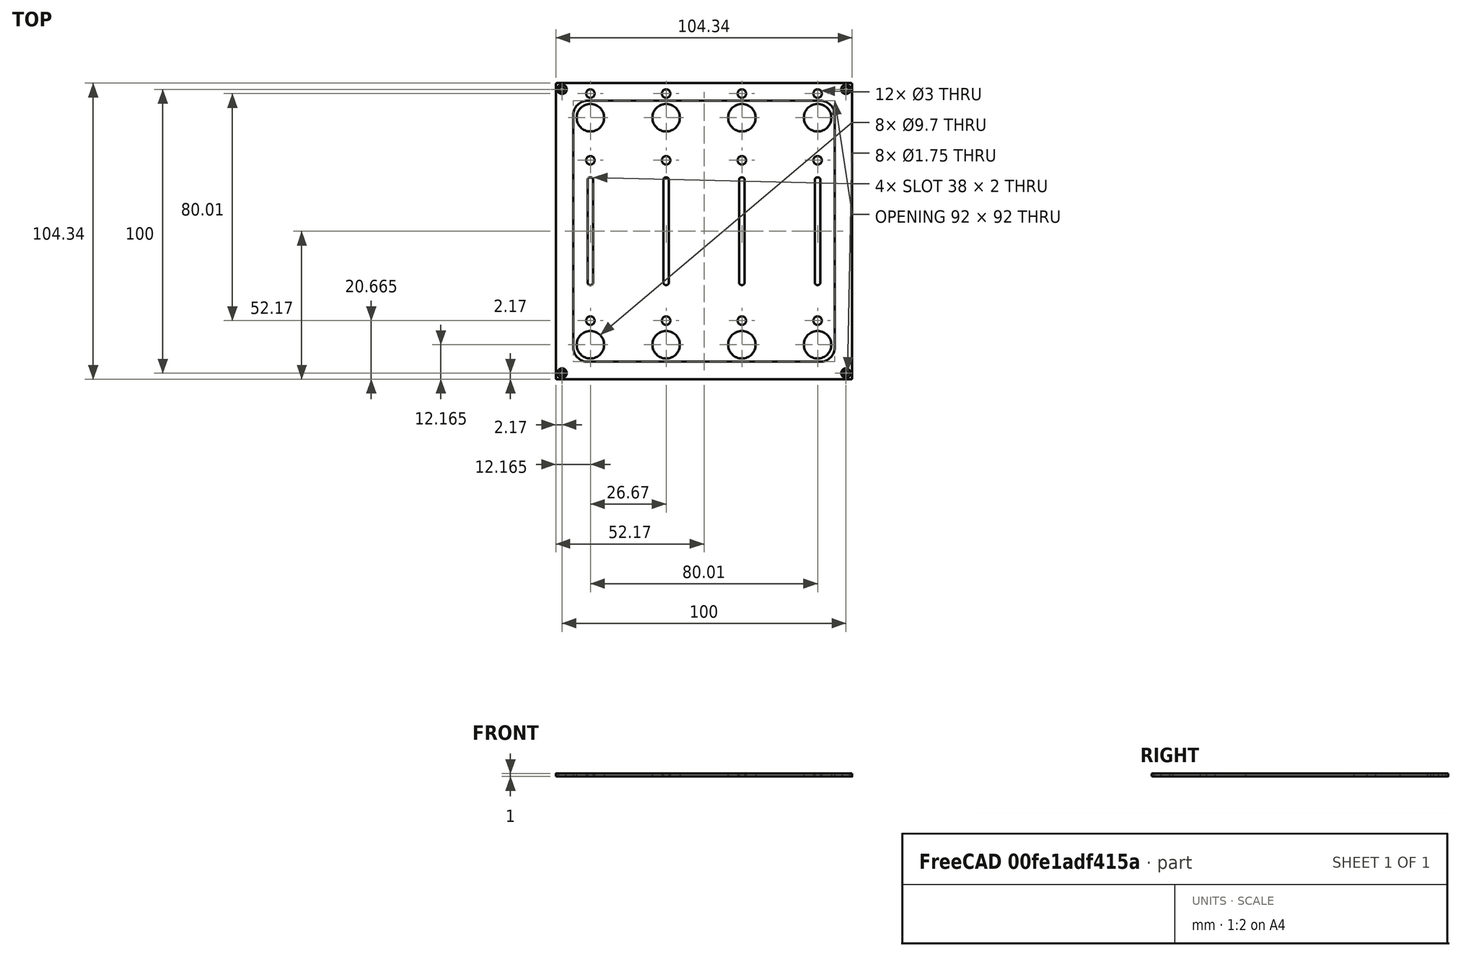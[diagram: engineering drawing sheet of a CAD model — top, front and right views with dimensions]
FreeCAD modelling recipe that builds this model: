
FCSTD DOCUMENT  (FreeCAD 0.21R33668 +26 (Git))
Label: grid_frontpanel
License: All rights reserved
LicenseURL: http://en.wikipedia.org/wiki/All_rights_reserved
objects: Sketcher::SketchObject×10, PartDesign::Hole×6, TechDraw::DrawProjGroupItem×4, PartDesign::Pocket×3, PartDesign::Body×3, TechDraw::DrawViewDimension×3, PartDesign::FeatureBase×2, TechDraw::DrawRichAnno×2, Spreadsheet::Sheet×1, PartDesign::Pad×1, TechDraw::DrawSVGTemplate×1, TechDraw::DrawProjGroup×1, TechDraw::DrawPage×1
note: 35 computed .brp shape members not serialized (recipe doc carries the construction recipe); baked Part::Feature solids carry a one-line shape summary decoded from their .brp

FEATURE [Spreadsheet::Sheet] Spreadsheet  label="dim"
  cells = A1='panel_length; B1(panel_length)=104.35; A2='panel_thickness; B2(panel_thickness)=1; A3='panel_radius; B3(panel_radius)==(104.35 - 103.6) / 2; A5='corner_drill_dist; B5(corner_drill_dist)=100; A6='corner_drill_dia; B6(corner_drill_dia)=1.75; A7='corner_drill_countersink; B7(corner_drill_countersink)=3.3; A9='undercut_width; B9(undercut_width)=1; A10='undercut_length; B10(undercut_length)=90; A11='undercut_offset; B11(undercut_offset)=1; A12='undercut_depth; B12(undercut_depth)=0.8; A14='ui_raster; B14(ui_raster)=26.67; A16='light_drill_dia; B16(light_drill_dia)=3; D16='old 2.9; A17='light_bore_dia; B17(light_bore_dia)=3.45; C17='check; D17='old 3.30; E17='DEPRICATED; A18='light_bore_depth; B18(light_bore_depth)=0.4; C18='check; D18='old 0.40; E18='DEPRICATED; A20='pot_drill_dia; B20(pot_drill_dia)=9.7; C20='check; D20='old 6.20; A21='pot_led_dist; B21(pot_led_dist)=8.5; B22=0; A23='but_drill_dia; B23(but_drill_dia)=9.7; A24='but_led_dist; B24(but_led_dist)=8.5; A26='fad_cutout_width; B26(fad_cutout_width)=2; C26='check; D26='old 1.50; A27='fad_cutout_length; B27(fad_cutout_length)=36; A28='fad_led_dist; B28(fad_led_dist)=25; A30='enc_drill_dia; B30(enc_drill_dia)=9.7; C30='check; D30='old 6.20; A31='enc_led_dist; B31(enc_led_dist)=8.5; A33='longfad_cutout_width; B33(longfad_cutout_width)=2; A34='longfad_cutout_length; B34(longfad_cutout_length)=66; A36='panel_chamfer; B36(panel_chamfer)=0.2; C36='UPDATE DRAWING
FEATURE [Sketcher::SketchObject] Sketch
  FullyConstrained = true
  MapMode = 5
  Support = -> [XY_Plane]
  expr: Constraints[12] = <<dim>>.panel_radius
  expr: Constraints[16] = <<dim>>.panel_length
  sketch-geometry (11):
    g0: LineSegment StartX=-51.8 StartY=52.175 StartZ=0 EndX=51.8 EndY=52.175 EndZ=0
    g1: LineSegment StartX=52.175 StartY=51.8 StartZ=0 EndX=52.175 EndY=-51.8 EndZ=0
    g2: LineSegment StartX=51.8 StartY=-52.175 StartZ=0 EndX=-51.8 EndY=-52.175 EndZ=0
    g3: LineSegment StartX=-52.175 StartY=-51.8 StartZ=0 EndX=-52.175 EndY=51.8 EndZ=0
    g4: ArcOfCircle CenterX=-51.8 CenterY=51.8 CenterZ=0 NormalX=0 NormalY=0 NormalZ=1 AngleXU=0 Radius=0.375 StartAngle=1.5708 EndAngle=3.14159
    g5: ArcOfCircle CenterX=51.8 CenterY=51.8 CenterZ=0 NormalX=0 NormalY=0 NormalZ=1 AngleXU=0 Radius=0.375 StartAngle=8.4e-15 EndAngle=1.5708
    g6: ArcOfCircle CenterX=51.8 CenterY=-51.8 CenterZ=0 NormalX=0 NormalY=0 NormalZ=1 AngleXU=0 Radius=0.375 StartAngle=4.71239 EndAngle=6.28319
    g7: ArcOfCircle CenterX=-51.8 CenterY=-51.8 CenterZ=0 NormalX=0 NormalY=0 NormalZ=1 AngleXU=0 Radius=0.375 StartAngle=3.14159 EndAngle=4.71239
    g8: LineSegment StartX=-51.8 StartY=51.8 StartZ=0 EndX=0 EndY=0 EndZ=0
    g9: LineSegment StartX=0 StartY=0 StartZ=0 EndX=51.8 EndY=51.8 EndZ=0
    g10: LineSegment StartX=0 StartY=0 StartZ=0 EndX=-51.8 EndY=-51.8 EndZ=0
  constraints (26):
    c: Horizontal(g0)
    c: Horizontal(g2)
    c: Vertical(g1)
    c: Vertical(g3)
    c: Tangent(g3,g4) = 1.5708
    c: Tangent(g0,g4) = 1.5708
    c: Tangent(g0,g5) = 1.5708
    c: Tangent(g1,g5) = 1.5708
    c: Tangent(g1,g6) = 1.5708
    c: Tangent(g2,g6) = 1.5708
    c: Tangent(g2,g7) = 1.5708
    c: Tangent(g3,g7) = 1.5708
    c: Radius(g4) = 0.375
    c: Equal(g4,g5)
    c: Equal(g4,g6)
    c: Equal(g4,g7)
    c: DistanceX(g3,g1) = 104.35
    c: Equal(g3,g0)
    c: Coincident(g8,g4)
    c: Coincident(g8,g-1)
    c: Coincident(g8,g9)
    c: Coincident(g9,g5)
    c: Coincident(g-1,g10)
    c: Coincident(g10,g7)
    c: Equal(g10,g8)
    c: Equal(g8,g9)
FEATURE [PartDesign::Pad] Pad  label="panel"
  AllowMultiFace = false
  Direction = (0,0,1)
  Length = 1
  Length2 = 100
  Profile = -> Sketch
  Reversed = true
  Type = 0
  expr: Length = <<dim>>.panel_thickness
FEATURE [Sketcher::SketchObject] Sketch001
  FullyConstrained = true
  MapMode = 5
  Support = -> [XY_Plane]
  expr: Constraints[13] = <<dim>>.corner_drill_dist
  sketch-geometry (9):
    g0: LineSegment StartX=-50 StartY=50 StartZ=0 EndX=-50 EndY=-50 EndZ=0
    g1: LineSegment StartX=-50 StartY=-50 StartZ=0 EndX=50 EndY=-50 EndZ=0
    g2: LineSegment StartX=50 StartY=-50 StartZ=0 EndX=50 EndY=50 EndZ=0
    g3: LineSegment StartX=50 StartY=50 StartZ=0 EndX=-50 EndY=50 EndZ=0
    g4: Circle CenterX=0 CenterY=0 CenterZ=0 NormalX=0 NormalY=0 NormalZ=1 AngleXU=0 Radius=70.7107
    g5: Circle CenterX=-50 CenterY=50 CenterZ=0 NormalX=0 NormalY=0 NormalZ=1 AngleXU=0 Radius=0.5
    g6: Circle CenterX=50 CenterY=50 CenterZ=0 NormalX=0 NormalY=0 NormalZ=1 AngleXU=0 Radius=0.5
    g7: Circle CenterX=50 CenterY=-50 CenterZ=0 NormalX=0 NormalY=0 NormalZ=1 AngleXU=0 Radius=0.5
    g8: Circle CenterX=-50 CenterY=-50 CenterZ=0 NormalX=0 NormalY=0 NormalZ=1 AngleXU=0 Radius=0.5
  constraints (22):
    c: Coincident(g0,g1)
    c: Coincident(g1,g2)
    c: Coincident(g2,g3)
    c: Coincident(g3,g0)
    c: Equal(g0,g1)
    c: Equal(g0,g2)
    c: Equal(g0,g3)
    c: PointOnObject(g0,g4)
    c: PointOnObject(g1,g4)
    c: PointOnObject(g2,g4)
    c: PointOnObject(g3,g4)
    c: Coincident(g4,g-1)
    c: Horizontal(g3)
    c: DistanceX(g3,g3) = 100
    c: Coincident(g5,g0)
    c: Coincident(g6,g2)
    c: Coincident(g7,g1)
    c: Coincident(g8,g0)
    c: Diameter(g8) = 1
    c: Equal(g8,g7)
    c: Equal(g8,g6)
    c: Equal(g8,g5)
FEATURE [Sketcher::SketchObject] Sketch002
  AttachmentOffset = pos=(0,0,-4.8) rot=(0,0,1;0rad)
  FullyConstrained = true
  MapMode = 5
  Placement = pos=(0,0,-4.8) rot=(0,0,1;0rad)
  Support = -> [XY_Plane]
  expr: .AttachmentOffset.Base.z = -<<dim>>.undercut_depth - 4
  expr: Constraints[91] = <<dim>>.undercut_length
  expr: Constraints[92] = <<dim>>.undercut_width
  expr: Constraints[93] = <<dim>>.panel_length / 2 - <<dim>>.undercut_offset - <<dim>>.undercut_width / 2
  sketch-geometry (40):
    g0: LineSegment StartX=-45 StartY=50.175 StartZ=0 EndX=45 EndY=50.175 EndZ=0
    g1: LineSegment StartX=-45 StartY=51.175 StartZ=0 EndX=45 EndY=51.175 EndZ=0
    g2: LineSegment StartX=-50.675 StartY=45 StartZ=0 EndX=0 EndY=0 EndZ=0
    g3: LineSegment StartX=0 StartY=0 StartZ=0 EndX=-50.675 EndY=-45 EndZ=0
    g4: LineSegment StartX=0 StartY=0 StartZ=0 EndX=-45 EndY=50.675 EndZ=0
    g5: LineSegment StartX=45 StartY=50.675 StartZ=0 EndX=0 EndY=0 EndZ=0
    g6: LineSegment StartX=0 StartY=0 StartZ=0 EndX=50.675 EndY=45 EndZ=0
    g7: LineSegment StartX=50.675 StartY=-45 StartZ=0 EndX=0 EndY=0 EndZ=0
    g8: LineSegment StartX=0 StartY=0 StartZ=0 EndX=45 EndY=-50.675 EndZ=0
    g9: LineSegment StartX=0 StartY=0 StartZ=0 EndX=-45 EndY=-50.675 EndZ=0
    g10: ArcOfCircle CenterX=45 CenterY=50.675 CenterZ=0 NormalX=0 NormalY=0 NormalZ=1 AngleXU=0 Radius=0.5 StartAngle=4.71239 EndAngle=6.28319
    g11: ArcOfCircle CenterX=45 CenterY=50.675 CenterZ=0 NormalX=0 NormalY=0 NormalZ=1 AngleXU=0 Radius=0.5 StartAngle=0 EndAngle=1.5708
    g12: LineSegment StartX=45 StartY=50.675 StartZ=0 EndX=45.5 EndY=50.675 EndZ=0
    g13: ArcOfCircle CenterX=-45 CenterY=50.675 CenterZ=0 NormalX=0 NormalY=0 NormalZ=1 AngleXU=0 Radius=0.5 StartAngle=3.14159 EndAngle=4.71239
    g14: ArcOfCircle CenterX=-45 CenterY=50.675 CenterZ=0 NormalX=0 NormalY=0 NormalZ=1 AngleXU=0 Radius=0.5 StartAngle=1.5708 EndAngle=3.14159
    g15: LineSegment StartX=-45.5 StartY=50.675 StartZ=0 EndX=-45 EndY=50.675 EndZ=0
    g16: LineSegment StartX=-45 StartY=-51.175 StartZ=0 EndX=45 EndY=-51.175 EndZ=0
    g17: LineSegment StartX=-45 StartY=-50.175 StartZ=0 EndX=45 EndY=-50.175 EndZ=0
    g18: ArcOfCircle CenterX=45 CenterY=-50.675 CenterZ=0 NormalX=0 NormalY=0 NormalZ=1 AngleXU=0 Radius=0.5 StartAngle=4.71239 EndAngle=6.28319
    g19: ArcOfCircle CenterX=45 CenterY=-50.675 CenterZ=0 NormalX=0 NormalY=0 NormalZ=1 AngleXU=0 Radius=0.5 StartAngle=0 EndAngle=1.5708
    g20: LineSegment StartX=45 StartY=-50.675 StartZ=0 EndX=45.5 EndY=-50.675 EndZ=0
    g21: ArcOfCircle CenterX=-45 CenterY=-50.675 CenterZ=0 NormalX=0 NormalY=0 NormalZ=1 AngleXU=0 Radius=0.5 StartAngle=3.14159 EndAngle=4.71239
    g22: ArcOfCircle CenterX=-45 CenterY=-50.675 CenterZ=0 NormalX=0 NormalY=0 NormalZ=1 AngleXU=0 Radius=0.5 StartAngle=1.5708 EndAngle=3.14159
    g23: LineSegment StartX=-45.5 StartY=-50.675 StartZ=0 EndX=-45 EndY=-50.675 EndZ=0
    g24: LineSegment StartX=51.175 StartY=-45 StartZ=0 EndX=51.175 EndY=45 EndZ=0
    g25: LineSegment StartX=50.175 StartY=-45 StartZ=0 EndX=50.175 EndY=45 EndZ=0
    g26: ArcOfCircle CenterX=50.675 CenterY=45 CenterZ=0 NormalX=0 NormalY=0 NormalZ=1 AngleXU=0 Radius=0.5 StartAngle=3.8e-15 EndAngle=1.5708
    g27: ArcOfCircle CenterX=50.675 CenterY=45 CenterZ=0 NormalX=0 NormalY=0 NormalZ=1 AngleXU=0 Radius=0.5 StartAngle=1.5708 EndAngle=3.14159
    g28: LineSegment StartX=50.675 StartY=45 StartZ=0 EndX=50.675 EndY=45.5 EndZ=0
    g29: ArcOfCircle CenterX=50.675 CenterY=-45 CenterZ=0 NormalX=0 NormalY=0 NormalZ=1 AngleXU=0 Radius=0.5 StartAngle=4.71239 EndAngle=6.28319
    g30: ArcOfCircle CenterX=50.675 CenterY=-45 CenterZ=0 NormalX=0 NormalY=0 NormalZ=1 AngleXU=0 Radius=0.5 StartAngle=3.14159 EndAngle=4.71239
    g31: LineSegment StartX=50.675 StartY=-45.5 StartZ=0 EndX=50.675 EndY=-45 EndZ=0
    g32: LineSegment StartX=-50.175 StartY=-45 StartZ=0 EndX=-50.175 EndY=45 EndZ=0
    g33: LineSegment StartX=-51.175 StartY=-45 StartZ=0 EndX=-51.175 EndY=45 EndZ=0
    g34: ArcOfCircle CenterX=-50.675 CenterY=45 CenterZ=0 NormalX=0 NormalY=0 NormalZ=1 AngleXU=0 Radius=0.5 StartAngle=1.4e-15 EndAngle=1.5708
    g35: ArcOfCircle CenterX=-50.675 CenterY=45 CenterZ=0 NormalX=0 NormalY=0 NormalZ=1 AngleXU=0 Radius=0.5 StartAngle=1.5708 EndAngle=3.14159
    g36: LineSegment StartX=-50.675 StartY=45 StartZ=0 EndX=-50.675 EndY=45.5 EndZ=0
    g37: ArcOfCircle CenterX=-50.675 CenterY=-45 CenterZ=0 NormalX=0 NormalY=0 NormalZ=1 AngleXU=0 Radius=0.5 StartAngle=4.71239 EndAngle=6.28319
    g38: ArcOfCircle CenterX=-50.675 CenterY=-45 CenterZ=0 NormalX=0 NormalY=0 NormalZ=1 AngleXU=0 Radius=0.5 StartAngle=3.14159 EndAngle=4.71239
    g39: LineSegment StartX=-50.675 StartY=-45.5 StartZ=0 EndX=-50.675 EndY=-45 EndZ=0
  constraints (96):
    c: Horizontal(g0)
    c: Coincident(g2,g-1)
    c: Coincident(g2,g3)
    c: Coincident(g-1,g4)
    c: Coincident(g5,g-1)
    c: Coincident(g5,g6)
    c: Coincident(g7,g-1)
    c: Coincident(g7,g8)
    c: Coincident(g-1,g9)
    c: Equal(g5,g6)
    c: Equal(g6,g8)
    c: Equal(g8,g7)
    c: Equal(g7,g9)
    c: Equal(g9,g3)
    c: Equal(g3,g2)
    c: Equal(g2,g4)
    c: Coincident(g10,g5)
    c: Coincident(g11,g10)
    c: Coincident(g11,g10)
    c: Tangent(g11,g1) = 1.5708
    c: Tangent(g10,g0) = -1.5708
    c: Coincident(g12,g10)
    c: Coincident(g12,g10)
    c: Horizontal(g12)
    c: Coincident(g13,g4)
    c: Coincident(g14,g13)
    c: Coincident(g14,g13)
    c: Tangent(g14,g1) = 1.5708
    c: Tangent(g13,g0) = -1.5708
    c: Coincident(g15,g13)
    c: Coincident(g15,g13)
    c: Horizontal(g15)
    c: Horizontal(g1)
    c: Horizontal(g16)
    c: Coincident(g19,g18)
    c: Coincident(g19,g18)
    c: Tangent(g19,g17) = 1.5708
    c: Tangent(g18,g16) = -1.5708
    c: Coincident(g20,g18)
    c: Coincident(g20,g18)
    c: Horizontal(g20)
    c: Coincident(g22,g21)
    c: Coincident(g22,g21)
    c: Tangent(g22,g17) = 1.5708
    c: Tangent(g21,g16) = -1.5708
    c: Coincident(g23,g21)
    c: Coincident(g23,g21)
    c: Horizontal(g23)
    c: Horizontal(g17)
    c: Coincident(g21,g9)
    c: Coincident(g8,g18)
    c: Equal(g22,g14)
    c: Equal(g17,g1)
    c: Coincident(g27,g26)
    c: Coincident(g27,g26)
    c: Tangent(g27,g25) = 1.5708
    c: Tangent(g26,g24) = -1.5708
    c: Coincident(g28,g26)
    c: Coincident(g28,g26)
    c: Coincident(g30,g29)
    c: Coincident(g30,g29)
    c: Tangent(g30,g25) = 1.5708
    c: Tangent(g29,g24) = -1.5708
    c: Coincident(g31,g29)
    c: Coincident(g31,g29)
    c: Vertical(g31)
    c: Vertical(g28)
    c: Vertical(g25)
    c: Vertical(g24)
    c: Coincident(g35,g34)
    c: Coincident(g35,g34)
    c: Tangent(g35,g33) = 1.5708
    c: Tangent(g34,g32) = -1.5708
    c: Coincident(g36,g34)
    c: Coincident(g36,g34)
    c: Coincident(g38,g37)
    c: Coincident(g38,g37)
    c: Tangent(g38,g33) = 1.5708
    c: Tangent(g37,g32) = -1.5708
    c: Coincident(g39,g37)
    c: Coincident(g39,g37)
    c: Vertical(g39)
    c: Vertical(g36)
    c: Vertical(g33)
    c: Vertical(g32)
    c: Coincident(g6,g26)
    c: Coincident(g7,g29)
    c: Equal(g25,g0)
    c: Equal(g11,g27)
    c: Equal(g1,g33)
    c: Equal(g35,g11)
    c: DistanceX(g13,g10) = 90
    c: Diameter(g13) = 1
    c: DistanceY(g-1,g13) = 50.675
    c: Coincident(g2,g34)
    c: Coincident(g3,g37)
FEATURE [Sketcher::SketchObject] Sketch007
  FullyConstrained = true
  MapMode = 5
  Support = -> [XY_Plane003]
  expr: Constraints[16] = <<dim>>.ui_raster * 1.5
  expr: Constraints[4] = <<dim>>.ui_raster
  sketch-geometry (9):
    g0: Circle CenterX=-40.005 CenterY=-40.005 CenterZ=0 NormalX=0 NormalY=0 NormalZ=1 AngleXU=0 Radius=2
    g1: Circle CenterX=-13.335 CenterY=-40.005 CenterZ=0 NormalX=0 NormalY=0 NormalZ=1 AngleXU=0 Radius=2
    g2: LineSegment StartX=-40.005 StartY=-40.005 StartZ=0 EndX=-13.335 EndY=-40.005 EndZ=0
    g3: Circle CenterX=13.335 CenterY=-40.005 CenterZ=0 NormalX=0 NormalY=0 NormalZ=1 AngleXU=0 Radius=2
    g4: LineSegment StartX=-13.335 StartY=-40.005 StartZ=0 EndX=13.335 EndY=-40.005 EndZ=0
    g5: Circle CenterX=40.005 CenterY=-40.005 CenterZ=0 NormalX=0 NormalY=0 NormalZ=1 AngleXU=0 Radius=2
    g6: LineSegment StartX=13.335 StartY=-40.005 StartZ=0 EndX=40.005 EndY=-40.005 EndZ=0
    g7: LineSegment StartX=-13.335 StartY=-40.005 StartZ=0 EndX=0 EndY=0 EndZ=0
    g8: LineSegment StartX=0 StartY=0 StartZ=0 EndX=13.335 EndY=-40.005 EndZ=0
  constraints (22):
    c: Diameter(g0) = 4
    c: Diameter(g1) = 4
    c: Coincident(g0,g2)
    c: Coincident(g1,g2)
    c: Distance(g2) = 26.67
    c: Angle(g2) = 0
    c: Diameter(g3) = 4
    c: Coincident(g1,g4)
    c: Coincident(g3,g4)
    c: Equal(g2,g4)
    c: Parallel(g4,g2)
    c: Diameter(g5) = 4
    c: Coincident(g3,g6)
    c: Coincident(g5,g6)
    c: Equal(g2,g6)
    c: Parallel(g6,g2)
    c: DistanceY(g0,g-1) = 40.005
    c: Coincident(g7,g1)
    c: Coincident(g7,g-1)
    c: Coincident(g7,g8)
    c: Coincident(g8,g3)
    c: Equal(g8,g7)
FEATURE [Sketcher::SketchObject] Sketch008
  FullyConstrained = true
  MapMode = 5
  Support = -> [XY_Plane003]
  expr: Constraints[21] = <<dim>>.ui_raster * 1.5
  expr: Constraints[22] = <<dim>>.but_led_dist
  expr: Constraints[4] = <<dim>>.ui_raster
  sketch-geometry (9):
    g0: Circle CenterX=-40.005 CenterY=-31.505 CenterZ=0 NormalX=0 NormalY=0 NormalZ=1 AngleXU=0 Radius=2
    g1: Circle CenterX=-13.335 CenterY=-31.505 CenterZ=0 NormalX=0 NormalY=0 NormalZ=1 AngleXU=0 Radius=2
    g2: LineSegment StartX=-40.005 StartY=-31.505 StartZ=0 EndX=-13.335 EndY=-31.505 EndZ=0
    g3: Circle CenterX=13.335 CenterY=-31.505 CenterZ=0 NormalX=0 NormalY=0 NormalZ=1 AngleXU=0 Radius=2
    g4: LineSegment StartX=-13.335 StartY=-31.505 StartZ=0 EndX=13.335 EndY=-31.505 EndZ=0
    g5: Circle CenterX=40.005 CenterY=-31.505 CenterZ=0 NormalX=0 NormalY=0 NormalZ=1 AngleXU=0 Radius=2
    g6: LineSegment StartX=13.335 StartY=-31.505 StartZ=0 EndX=40.005 EndY=-31.505 EndZ=0
    g7: LineSegment StartX=-13.335 StartY=-31.505 StartZ=0 EndX=0 EndY=-40.005 EndZ=0
    g8: LineSegment StartX=0 StartY=-40.005 StartZ=0 EndX=13.335 EndY=-31.505 EndZ=0
  constraints (23):
    c: Diameter(g0) = 4
    c: Diameter(g1) = 4
    c: Coincident(g0,g2)
    c: Coincident(g1,g2)
    c: Distance(g2) = 26.67
    c: Angle(g2) = 0
    c: Diameter(g3) = 4
    c: Coincident(g1,g4)
    c: Coincident(g3,g4)
    c: Equal(g2,g4)
    c: Parallel(g4,g2)
    c: Diameter(g5) = 4
    c: Coincident(g3,g6)
    c: Coincident(g5,g6)
    c: Equal(g2,g6)
    c: Parallel(g6,g2)
    c: Coincident(g7,g1)
    c: PointOnObject(g7,g-2)
    c: Coincident(g8,g7)
    c: Coincident(g8,g3)
    c: Equal(g8,g7)
    c: DistanceY(g7,g-1) = 40.005
    c: DistanceY(g7,g0) = 8.5
FEATURE [Sketcher::SketchObject] Sketch009
  FullyConstrained = true
  MapMode = 5
  Support = -> [XY_Plane003]
  expr: Constraints[21] = <<dim>>.ui_raster * 1.5
  expr: Constraints[4] = <<dim>>.ui_raster
  sketch-geometry (9):
    g0: Circle CenterX=-40.005 CenterY=40.005 CenterZ=0 NormalX=0 NormalY=0 NormalZ=1 AngleXU=0 Radius=2
    g1: Circle CenterX=-13.335 CenterY=40.005 CenterZ=0 NormalX=0 NormalY=0 NormalZ=1 AngleXU=0 Radius=2
    g2: LineSegment StartX=-40.005 StartY=40.005 StartZ=0 EndX=-13.335 EndY=40.005 EndZ=0
    g3: Circle CenterX=13.335 CenterY=40.005 CenterZ=0 NormalX=0 NormalY=0 NormalZ=1 AngleXU=0 Radius=2
    g4: LineSegment StartX=-13.335 StartY=40.005 StartZ=0 EndX=13.335 EndY=40.005 EndZ=0
    g5: Circle CenterX=40.005 CenterY=40.005 CenterZ=0 NormalX=0 NormalY=0 NormalZ=1 AngleXU=0 Radius=2
    g6: LineSegment StartX=13.335 StartY=40.005 StartZ=0 EndX=40.005 EndY=40.005 EndZ=0
    g7: LineSegment StartX=-13.335 StartY=40.005 StartZ=0 EndX=0 EndY=0 EndZ=0
    g8: LineSegment StartX=0 StartY=0 StartZ=0 EndX=13.335 EndY=40.005 EndZ=0
  constraints (22):
    c: Diameter(g0) = 4
    c: Diameter(g1) = 4
    c: Coincident(g0,g2)
    c: Coincident(g1,g2)
    c: Distance(g2) = 26.67
    c: Angle(g2) = 0
    c: Diameter(g3) = 4
    c: Coincident(g1,g4)
    c: Coincident(g3,g4)
    c: Equal(g2,g4)
    c: Parallel(g4,g2)
    c: Diameter(g5) = 4
    c: Coincident(g3,g6)
    c: Coincident(g5,g6)
    c: Equal(g2,g6)
    c: Parallel(g6,g2)
    c: Coincident(g7,g1)
    c: Coincident(g7,g-1)
    c: Coincident(g7,g8)
    c: Coincident(g8,g3)
    c: Equal(g7,g8)
    c: DistanceY(g-1,g0) = 40.005
FEATURE [Sketcher::SketchObject] Sketch010
  FullyConstrained = true
  MapMode = 5
  Support = -> [XY_Plane003]
  expr: Constraints[20] = <<dim>>.ui_raster * 1.5
  expr: Constraints[21] = <<dim>>.pot_led_dist
  expr: Constraints[4] = <<dim>>.ui_raster
  sketch-geometry (9):
    g0: Circle CenterX=-40.005 CenterY=48.505 CenterZ=0 NormalX=0 NormalY=0 NormalZ=1 AngleXU=0 Radius=2
    g1: Circle CenterX=-13.335 CenterY=48.505 CenterZ=0 NormalX=0 NormalY=0 NormalZ=1 AngleXU=0 Radius=2
    g2: LineSegment StartX=-40.005 StartY=48.505 StartZ=0 EndX=-13.335 EndY=48.505 EndZ=0
    g3: Circle CenterX=13.335 CenterY=48.505 CenterZ=0 NormalX=0 NormalY=0 NormalZ=1 AngleXU=0 Radius=2
    g4: LineSegment StartX=-13.335 StartY=48.505 StartZ=0 EndX=13.335 EndY=48.505 EndZ=0
    g5: Circle CenterX=40.005 CenterY=48.505 CenterZ=0 NormalX=0 NormalY=0 NormalZ=1 AngleXU=0 Radius=2
    g6: LineSegment StartX=13.335 StartY=48.505 StartZ=0 EndX=40.005 EndY=48.505 EndZ=0
    g7: LineSegment StartX=-13.335 StartY=48.505 StartZ=0 EndX=0 EndY=40.005 EndZ=0
    g8: LineSegment StartX=0 StartY=40.005 StartZ=0 EndX=13.335 EndY=48.505 EndZ=0
  constraints (23):
    c: Diameter(g0) = 4
    c: Diameter(g1) = 4
    c: Coincident(g0,g2)
    c: Coincident(g1,g2)
    c: Distance(g2) = 26.67
    c: Angle(g2) = 0
    c: Diameter(g3) = 4
    c: Coincident(g1,g4)
    c: Coincident(g3,g4)
    c: Equal(g2,g4)
    c: Parallel(g4,g2)
    c: Diameter(g5) = 4
    c: Coincident(g3,g6)
    c: Coincident(g5,g6)
    c: Equal(g2,g6)
    c: Parallel(g6,g2)
    c: Coincident(g7,g1)
    c: PointOnObject(g7,g-2)
    c: Coincident(g7,g8)
    c: Coincident(g8,g3)
    c: DistanceY(g-1,g7) = 40.005
    c: DistanceY(g7,g1) = 8.5
    c: Equal(g8,g7)
FEATURE [Sketcher::SketchObject] Sketch011
  FullyConstrained = true
  MapMode = 5
  Support = -> [XY_Plane003]
  expr: Constraints[17] = <<dim>>.ui_raster
  expr: Constraints[6] = <<dim>>.fad_cutout_width
  expr: Constraints[7] = <<dim>>.fad_cutout_length
  sketch-geometry (22):
    g0: ArcOfCircle CenterX=-40.005 CenterY=18 CenterZ=0 NormalX=0 NormalY=0 NormalZ=1 AngleXU=0 Radius=1 StartAngle=-9e-16 EndAngle=3.14159
    g1: ArcOfCircle CenterX=-40.005 CenterY=-18 CenterZ=0 NormalX=0 NormalY=0 NormalZ=1 AngleXU=0 Radius=1 StartAngle=3.14159 EndAngle=6.28319
    g2: LineSegment StartX=-41.005 StartY=18 StartZ=0 EndX=-41.005 EndY=-18 EndZ=0
    g3: LineSegment StartX=-39.005 StartY=18 StartZ=0 EndX=-39.005 EndY=-18 EndZ=0
    g4: ArcOfCircle CenterX=-13.335 CenterY=18 CenterZ=0 NormalX=0 NormalY=0 NormalZ=1 AngleXU=0 Radius=1 StartAngle=0 EndAngle=3.14159
    g5: ArcOfCircle CenterX=-13.335 CenterY=-18 CenterZ=0 NormalX=0 NormalY=0 NormalZ=1 AngleXU=0 Radius=1 StartAngle=3.14159 EndAngle=6.28319
    g6: LineSegment StartX=-14.335 StartY=18 StartZ=0 EndX=-14.335 EndY=-18 EndZ=0
    g7: LineSegment StartX=-12.335 StartY=18 StartZ=0 EndX=-12.335 EndY=-18 EndZ=0
    g8: LineSegment StartX=-39.005 StartY=18 StartZ=0 EndX=-12.335 EndY=18 EndZ=0
    g9: ArcOfCircle CenterX=13.335 CenterY=18 CenterZ=0 NormalX=0 NormalY=0 NormalZ=1 AngleXU=0 Radius=1 StartAngle=1e-15 EndAngle=3.14159
    g10: ArcOfCircle CenterX=13.335 CenterY=-18 CenterZ=0 NormalX=0 NormalY=0 NormalZ=1 AngleXU=0 Radius=1 StartAngle=3.14159 EndAngle=6.28319
    g11: LineSegment StartX=12.335 StartY=18 StartZ=0 EndX=12.335 EndY=-18 EndZ=0
    g12: LineSegment StartX=14.335 StartY=18 StartZ=0 EndX=14.335 EndY=-18 EndZ=0
    g13: LineSegment StartX=-12.335 StartY=18 StartZ=0 EndX=14.335 EndY=18 EndZ=0
    g14: ArcOfCircle CenterX=40.005 CenterY=18 CenterZ=0 NormalX=0 NormalY=0 NormalZ=1 AngleXU=0 Radius=1 StartAngle=8e-16 EndAngle=3.14159
    g15: ArcOfCircle CenterX=40.005 CenterY=-18 CenterZ=0 NormalX=0 NormalY=0 NormalZ=1 AngleXU=0 Radius=1 StartAngle=3.14159 EndAngle=6.28319
    g16: LineSegment StartX=39.005 StartY=18 StartZ=0 EndX=39.005 EndY=-18 EndZ=0
    g17: LineSegment StartX=41.005 StartY=18 StartZ=0 EndX=41.005 EndY=-18 EndZ=0
    g18: LineSegment StartX=14.335 StartY=18 StartZ=0 EndX=41.005 EndY=18 EndZ=0
    g19: LineSegment StartX=-13.335 StartY=18 StartZ=0 EndX=0 EndY=0 EndZ=0
    g20: LineSegment StartX=0 StartY=0 StartZ=0 EndX=13.335 EndY=18 EndZ=0
    g21: LineSegment StartX=0 StartY=0 StartZ=0 EndX=-13.335 EndY=-18 EndZ=0
  constraints (52):
    c: Tangent(g0,g3) = 1.5708
    c: Tangent(g0,g2) = -1.5708
    c: Tangent(g2,g1) = -1.5708
    c: Tangent(g3,g1) = 1.5708
    c: Vertical(g2)
    c: Equal(g0,g1)
    c: DistanceX(g0,g0) = 2
    c: DistanceY(g1,g0) = 36
    c: Tangent(g4,g7) = 1.5708
    c: Tangent(g4,g6) = -1.5708
    c: Tangent(g6,g5) = -1.5708
    c: Tangent(g7,g5) = 1.5708
    c: Vertical(g6)
    c: Equal(g4,g5)
    c: DistanceY(g5,g4) = 36
    c: Coincident(g0,g8)
    c: Coincident(g4,g8)
    c: Distance(g8) = 26.67
    c: Angle(g8) = 0
    c: Tangent(g9,g12) = 1.5708
    c: Tangent(g9,g11) = -1.5708
    c: Tangent(g11,g10) = -1.5708
    c: Tangent(g12,g10) = 1.5708
    c: Vertical(g11)
    c: Equal(g9,g10)
    c: DistanceY(g10,g9) = 36
    c: Coincident(g4,g13)
    c: Coincident(g9,g13)
    c: Equal(g8,g13)
    c: Parallel(g13,g8)
    c: Tangent(g14,g17) = 1.5708
    c: Tangent(g14,g16) = -1.5708
    c: Tangent(g16,g15) = -1.5708
    c: Tangent(g17,g15) = 1.5708
    c: Vertical(g16)
    c: Equal(g14,g15)
    c: DistanceY(g15,g14) = 36
    c: Coincident(g9,g18)
    c: Coincident(g14,g18)
    c: Equal(g8,g18)
    c: Parallel(g18,g8)
    c: Coincident(g19,g4)
    c: Coincident(g19,g-1)
    c: Coincident(g19,g20)
    c: Coincident(g20,g9)
    c: Coincident(g-1,g21)
    c: Coincident(g21,g5)
    c: Equal(g21,g19)
    c: Equal(g19,g20)
    c: Equal(g4,g9)
    c: Equal(g9,g14)
    c: Equal(g14,g0)
FEATURE [Sketcher::SketchObject] Sketch012
  FullyConstrained = true
  MapMode = 5
  Support = -> [XY_Plane003]
  expr: Constraints[21] = <<dim>>.fad_led_dist
  expr: Constraints[4] = <<dim>>.ui_raster
  sketch-geometry (9):
    g0: Circle CenterX=-40.005 CenterY=25 CenterZ=0 NormalX=0 NormalY=0 NormalZ=1 AngleXU=0 Radius=2
    g1: Circle CenterX=-13.335 CenterY=25 CenterZ=0 NormalX=0 NormalY=0 NormalZ=1 AngleXU=0 Radius=2
    g2: LineSegment StartX=-40.005 StartY=25 StartZ=0 EndX=-13.335 EndY=25 EndZ=0
    g3: Circle CenterX=13.335 CenterY=25 CenterZ=0 NormalX=0 NormalY=0 NormalZ=1 AngleXU=0 Radius=2
    g4: LineSegment StartX=-13.335 StartY=25 StartZ=0 EndX=13.335 EndY=25 EndZ=0
    g5: Circle CenterX=40.005 CenterY=25 CenterZ=0 NormalX=0 NormalY=0 NormalZ=1 AngleXU=0 Radius=2
    g6: LineSegment StartX=13.335 StartY=25 StartZ=0 EndX=40.005 EndY=25 EndZ=0
    g7: LineSegment StartX=-13.335 StartY=25 StartZ=0 EndX=0 EndY=0 EndZ=0
    g8: LineSegment StartX=0 StartY=0 StartZ=0 EndX=13.335 EndY=25 EndZ=0
  constraints (22):
    c: Diameter(g0) = 4
    c: Diameter(g1) = 4
    c: Coincident(g0,g2)
    c: Coincident(g1,g2)
    c: Distance(g2) = 26.67
    c: Angle(g2) = 0
    c: Diameter(g3) = 4
    c: Coincident(g1,g4)
    c: Coincident(g3,g4)
    c: Equal(g2,g4)
    c: Parallel(g4,g2)
    c: Diameter(g5) = 4
    c: Coincident(g3,g6)
    c: Coincident(g5,g6)
    c: Equal(g2,g6)
    c: Parallel(g6,g2)
    c: Coincident(g7,g1)
    c: Coincident(g7,g-1)
    c: Coincident(g7,g8)
    c: Coincident(g8,g3)
    c: Equal(g8,g7)
    c: DistanceY(g-1,g0) = 25
FEATURE [Sketcher::SketchObject] Sketch019
  FullyConstrained = true
  MapMode = 5
  Support = -> [XY_Plane009]
  sketch-geometry (11):
    g0: LineSegment StartX=-41 StartY=46 StartZ=0 EndX=41 EndY=46 EndZ=0
    g1: LineSegment StartX=46 StartY=41 StartZ=0 EndX=46 EndY=-41 EndZ=0
    g2: LineSegment StartX=41 StartY=-46 StartZ=0 EndX=-41 EndY=-46 EndZ=0
    g3: LineSegment StartX=-46 StartY=-41 StartZ=0 EndX=-46 EndY=41 EndZ=0
    g4: ArcOfCircle CenterX=-41 CenterY=41 CenterZ=0 NormalX=0 NormalY=0 NormalZ=1 AngleXU=0 Radius=5 StartAngle=1.5708 EndAngle=3.14159
    g5: ArcOfCircle CenterX=41 CenterY=41 CenterZ=0 NormalX=0 NormalY=0 NormalZ=1 AngleXU=0 Radius=5 StartAngle=0 EndAngle=1.5708
    g6: ArcOfCircle CenterX=41 CenterY=-41 CenterZ=0 NormalX=0 NormalY=0 NormalZ=1 AngleXU=0 Radius=5 StartAngle=4.71239 EndAngle=6.28319
    g7: ArcOfCircle CenterX=-41 CenterY=-41 CenterZ=0 NormalX=0 NormalY=0 NormalZ=1 AngleXU=0 Radius=5 StartAngle=3.14159 EndAngle=4.71239
    g8: LineSegment StartX=-41 StartY=-41 StartZ=0 EndX=0 EndY=0 EndZ=0
    g9: LineSegment StartX=0 StartY=0 StartZ=0 EndX=-41 EndY=41 EndZ=0
    g10: LineSegment StartX=41 StartY=41 StartZ=0 EndX=0 EndY=0 EndZ=0
  constraints (26):
    c: Horizontal(g0)
    c: Horizontal(g2)
    c: Vertical(g1)
    c: Vertical(g3)
    c: Tangent(g3,g4) = 1.5708
    c: Tangent(g0,g4) = 1.5708
    c: Tangent(g0,g5) = 1.5708
    c: Tangent(g1,g5) = 1.5708
    c: Tangent(g1,g6) = 1.5708
    c: Tangent(g2,g6) = 1.5708
    c: Tangent(g2,g7) = 1.5708
    c: Tangent(g3,g7) = 1.5708
    c: Equal(g7,g4)
    c: Equal(g4,g5)
    c: Equal(g5,g6)
    c: Equal(g0,g3)
    c: Radius(g5) = 5
    c: Coincident(g8,g7)
    c: Coincident(g8,g-1)
    c: Coincident(g8,g9)
    c: Coincident(g9,g4)
    c: Coincident(g10,g5)
    c: Coincident(g10,g-1)
    c: Equal(g8,g9)
    c: Equal(g9,g10)
    c: DistanceX(g3,g1) = 92
FEATURE [TechDraw::DrawSVGTemplate] Template002
  EditableTexts = AUTHOR_NAME=Intech Studio Ltd; DN=DN; DRAWING_TITLE=PBF4 Frontpanel; FC-DATE=2022.07.30.; FC-REV=REV A; FC-SC=1:1; FC-SH=1/1; FC-SI=A2; PN=PBF4-Alu; SI-1=All dimensions in millimeters unless otherwise stated!
  Height = 420
  Orientation = 1
  Width = 594
FEATURE [PartDesign::Pocket] Pocket
  AllowMultiFace = false
  BaseFeature = -> Pad
  Direction = (0,0,-1)
  Length = 5
  Length2 = 100
  Profile = -> Sketch002
  Type = 1
FEATURE [PartDesign::Hole] Hole
  BaseFeature = -> Pocket
  CustomThreadClearance = 0
  Depth = 298.105
  DepthType = 1
  Diameter = 1.75
  DrillForDepth = false
  DrillPoint = 1
  DrillPointAngle = 118
  HoleCutCountersinkAngle = 90
  HoleCutCustomValues = false
  HoleCutDepth = 0
  HoleCutDiameter = 3.3
  HoleCutType = 2
  ModelThread = false
  Profile = -> Sketch001
  Tapered = false
  TaperedAngle = 90
  ThreadClass = 0
  ThreadDepth = 298.105
  ThreadDepthType = 0
  ThreadDirection = 0
  ThreadFit = 0
  ThreadSize = 0
  ThreadType = 0
  Threaded = false
  UseCustomThreadClearance = false
  expr: Diameter = <<dim>>.corner_drill_dia
  expr: HoleCutDiameter = <<dim>>.corner_drill_countersink
FEATURE [PartDesign::Body] Body  label="Base"
  Group = -> [Sketch,Pad,Sketch001,Sketch002,Pocket,Hole]
  Origin = -> Origin
  Tip = -> Hole
FEATURE [PartDesign::FeatureBase] Clone002
  BaseFeature = -> Body
FEATURE [PartDesign::Hole] Hole005  label="PBF4_ButtonHole"
  AllowMultiFace = false
  BaseFeature = -> Clone002
  CustomThreadClearance = 0
  Depth = 25
  DepthType = 1
  Diameter = 9.7
  DrillForDepth = false
  DrillPoint = 0
  DrillPointAngle = 118
  HoleCutCountersinkAngle = 90
  HoleCutCustomValues = false
  HoleCutDepth = 0
  HoleCutDiameter = 0
  HoleCutType = 0
  ModelThread = false
  Profile = -> Sketch007
  Tapered = false
  TaperedAngle = 90
  ThreadClass = 0
  ThreadDepth = 23.5
  ThreadDepthType = 0
  ThreadDirection = 0
  ThreadFit = 0
  ThreadSize = 0
  ThreadType = 0
  Threaded = false
  UseCustomThreadClearance = false
  expr: Diameter = <<dim>>.but_drill_dia
FEATURE [PartDesign::Hole] Hole006  label="PBF4_ButtonLight"
  AllowMultiFace = false
  BaseFeature = -> Hole005
  CustomThreadClearance = 0
  Depth = 25
  DepthType = 1
  Diameter = 3
  DrillForDepth = false
  DrillPoint = 0
  DrillPointAngle = 118
  HoleCutCountersinkAngle = 90
  HoleCutCustomValues = false
  HoleCutDepth = 0.4
  HoleCutDiameter = 3.45
  HoleCutType = 0
  ModelThread = false
  Profile = -> Sketch008
  Tapered = false
  TaperedAngle = 90
  ThreadClass = 0
  ThreadDepth = 23.5
  ThreadDepthType = 0
  ThreadDirection = 0
  ThreadFit = 0
  ThreadSize = 0
  ThreadType = 0
  Threaded = false
  UseCustomThreadClearance = false
  expr: Diameter = <<dim>>.light_drill_dia
  expr: HoleCutDepth = <<dim>>.light_bore_depth
  expr: HoleCutDiameter = <<dim>>.light_bore_dia
FEATURE [PartDesign::Hole] Hole007
  AllowMultiFace = false
  BaseFeature = -> Hole006
  CustomThreadClearance = 0
  Depth = 25
  DepthType = 1
  Diameter = 9.7
  DrillForDepth = false
  DrillPoint = 0
  DrillPointAngle = 118
  HoleCutCountersinkAngle = 90
  HoleCutCustomValues = false
  HoleCutDepth = 0
  HoleCutDiameter = 0
  HoleCutType = 0
  ModelThread = false
  Profile = -> Sketch009
  Tapered = false
  TaperedAngle = 90
  ThreadClass = 0
  ThreadDepth = 23.5
  ThreadDepthType = 0
  ThreadDirection = 0
  ThreadFit = 0
  ThreadSize = 0
  ThreadType = 0
  Threaded = false
  UseCustomThreadClearance = false
  expr: Diameter = <<dim>>.pot_drill_dia
FEATURE [PartDesign::Hole] Hole008
  AllowMultiFace = false
  BaseFeature = -> Hole007
  CustomThreadClearance = 0
  Depth = 25
  DepthType = 1
  Diameter = 3
  DrillForDepth = false
  DrillPoint = 1
  DrillPointAngle = 118
  HoleCutCountersinkAngle = 90
  HoleCutCustomValues = false
  HoleCutDepth = 0.4
  HoleCutDiameter = 3.45
  HoleCutType = 0
  ModelThread = false
  Profile = -> Sketch010
  Tapered = false
  TaperedAngle = 90
  ThreadClass = 0
  ThreadDepth = 23.5
  ThreadDepthType = 0
  ThreadDirection = 0
  ThreadFit = 0
  ThreadSize = 0
  ThreadType = 0
  Threaded = false
  UseCustomThreadClearance = false
  expr: Diameter = <<dim>>.light_drill_dia
  expr: HoleCutDepth = <<dim>>.light_bore_depth
  expr: HoleCutDiameter = <<dim>>.light_bore_dia
FEATURE [PartDesign::Pocket] Pocket001
  AllowMultiFace = false
  BaseFeature = -> Hole008
  Direction = (0,0,-1)
  Length = 5
  Length2 = 100
  Profile = -> Sketch011
  Type = 1
FEATURE [PartDesign::Hole] Hole009
  AllowMultiFace = false
  BaseFeature = -> Pocket001
  CustomThreadClearance = 0
  Depth = 25
  DepthType = 1
  Diameter = 3
  DrillForDepth = false
  DrillPoint = 0
  DrillPointAngle = 118
  HoleCutCountersinkAngle = 90
  HoleCutCustomValues = false
  HoleCutDepth = 0.4
  HoleCutDiameter = 3.45
  HoleCutType = 0
  ModelThread = false
  Profile = -> Sketch012
  Tapered = false
  TaperedAngle = 90
  ThreadClass = 0
  ThreadDepth = 23.5
  ThreadDepthType = 0
  ThreadDirection = 0
  ThreadFit = 0
  ThreadSize = 0
  ThreadType = 0
  Threaded = false
  UseCustomThreadClearance = false
  expr: Diameter = <<dim>>.light_drill_dia
  expr: HoleCutDepth = <<dim>>.light_bore_depth
  expr: HoleCutDiameter = <<dim>>.light_bore_dia
FEATURE [PartDesign::Body] Body003  label="PBF4"
  BaseFeature = -> Body
  Group = -> [Clone002,Sketch007,Hole005,Sketch008,Hole006,Sketch009,Hole007,Sketch010,Hole008,Sketch011,Pocket001,Sketch012,Hole009]
  Origin = -> Origin003
  Tip = -> Hole009
FEATURE [PartDesign::FeatureBase] Clone007
  BaseFeature = -> Body
FEATURE [PartDesign::Pocket] Pocket005
  BaseFeature = -> Clone007
  Direction = (0,0,-1)
  Length = 5
  Length2 = 100
  Profile = -> Sketch019
  Type = 1
FEATURE [PartDesign::Body] Body009  label="XY"
  BaseFeature = -> Body
  Group = -> [Clone007,Sketch019,Pocket005]
  Origin = -> Origin009
  Tip = -> Pocket005
FEATURE [TechDraw::DrawProjGroupItem] ProjItem  label="Front"
  CoarseView = false
  Direction = (0,0,1)
  Focus = 100
  HardHidden = false
  IsoCount = 0
  IsoHidden = false
  IsoVisible = false
  LockPosition = true
  Perspective = false
  Rotation = 0
  RotationVector = (1,0,0)
  ScaleType = 2
  ScrubCount = 0
  SeamHidden = false
  SeamVisible = false
  SmoothHidden = false
  SmoothVisible = true
  Source = -> [Body003]
  Type = 0
  X = 0
  XDirection = (1,0,0)
  Y = 0
FEATURE [TechDraw::DrawProjGroupItem] ProjItem003  label="Right"
  CoarseView = false
  Direction = (1,0,1e-16)
  Focus = 100
  HardHidden = false
  IsoCount = 0
  IsoHidden = false
  IsoVisible = false
  LockPosition = false
  Perspective = false
  Rotation = 0
  RotationVector = (1,0,0)
  ScaleType = 2
  ScrubCount = 0
  SeamHidden = false
  SeamVisible = false
  SmoothHidden = false
  SmoothVisible = true
  Source = -> [Body003]
  Type = 2
  X = -72.675
  XDirection = (1e-16,0,-1)
  Y = 0
FEATURE [TechDraw::DrawProjGroupItem] ProjItem004  label="Rear"
  CoarseView = false
  Direction = (0,0,-1)
  Focus = 100
  HardHidden = false
  IsoCount = 0
  IsoHidden = false
  IsoVisible = false
  LockPosition = false
  Perspective = false
  Rotation = 0
  RotationVector = (1,0,0)
  ScaleType = 2
  ScrubCount = 0
  SeamHidden = false
  SeamVisible = false
  SmoothHidden = false
  SmoothVisible = true
  Source = -> [Body003]
  Type = 3
  X = 145.35
  XDirection = (-1,0,0)
  Y = 0
FEATURE [TechDraw::DrawProjGroupItem] ProjItem005  label="Left"
  CoarseView = false
  Direction = (-1,0,1e-16)
  Focus = 100
  HardHidden = false
  IsoCount = 0
  IsoHidden = false
  IsoVisible = false
  LockPosition = false
  Perspective = false
  Rotation = 0
  RotationVector = (1,0,0)
  ScaleType = 2
  ScrubCount = 0
  SeamHidden = false
  SeamVisible = false
  SmoothHidden = false
  SmoothVisible = true
  Source = -> [Body003]
  Type = 1
  X = 72.675
  XDirection = (1e-16,0,1)
  Y = 0
FEATURE [TechDraw::DrawProjGroup] ProjGroup
  Anchor = -> ProjItem
  AutoDistribute = true
  LockPosition = false
  ProjectionType = 0
  Rotation = 0
  ScaleType = 0
  Source = -> [Body003]
  Views = -> [ProjItem,ProjItem003,ProjItem004,ProjItem005]
  X = 297
  Y = 210
  spacingX = 20
  spacingY = 20
FEATURE [TechDraw::DrawViewDimension] Dimension
  AngleOverride = false
  Arbitrary = false
  ArbitraryTolerances = false
  EqualTolerance = true
  ExtensionAngle = 0
  FormatSpec = %.2w
  FormatSpecOverTolerance = %+.2w
  FormatSpecUnderTolerance = %+.2w
  Inverted = false
  LineAngle = 0
  LockPosition = false
  MeasureType = 1
  OverTolerance = 0
  References2D = -> [ProjItem]
  Rotation = 0
  ScaleType = 0
  TheoreticalExact = false
  Type = 1
  UnderTolerance = 0
  X = -0.928628
  Y = 67.4556
FEATURE [TechDraw::DrawViewDimension] Dimension001
  AngleOverride = false
  Arbitrary = false
  ArbitraryTolerances = false
  EqualTolerance = true
  ExtensionAngle = 0
  FormatSpec = %.2w
  FormatSpecOverTolerance = %+.2w
  FormatSpecUnderTolerance = %+.2w
  Inverted = false
  LineAngle = 0
  LockPosition = false
  MeasureType = 1
  OverTolerance = 0
  References2D = -> [ProjItem]
  Rotation = 0
  ScaleType = 0
  TheoreticalExact = false
  Type = 2
  UnderTolerance = 0
  X = -62.4792
  Y = 3.11909
FEATURE [TechDraw::DrawViewDimension] Dimension002
  AngleOverride = false
  Arbitrary = false
  ArbitraryTolerances = false
  EqualTolerance = true
  ExtensionAngle = 0
  FormatSpec = R%.2w
  FormatSpecOverTolerance = %+.2w
  FormatSpecUnderTolerance = %+.2w
  Inverted = false
  LineAngle = 0
  LockPosition = false
  MeasureType = 1
  OverTolerance = 0
  References2D = -> [ProjItem004]
  Rotation = 0
  ScaleType = 0
  TheoreticalExact = false
  Type = 4
  UnderTolerance = 0
  X = 68.4999
  Y = 66.6641
FEATURE [TechDraw::DrawRichAnno] RichTextAnnotation
  AnnoText = <blob: 4790 chars omitted>
  LockPosition = false
  MaxWidth = -1
  Rotation = 0
  ScaleType = 0
  ShowFrame = false
  X = 106.054
  Y = 118.63
FEATURE [TechDraw::DrawRichAnno] RichTextAnnotation001
  AnnoText = <!DOCTYPE HTML PUBLIC "-//W3C//DTD HTML 4.0//EN" "http://www.w3.org/TR/REC-html40/strict.dtd">\n<html><head><meta name="qrichtext" content="1" /><style type="text/css">\np, li { white-space: pre-wrap; }\n</style></head><body style=" font-family:'Sans Serif'; font-size:9pt; font-weight:400; font-style:normal;">\n<p style=" margin-top:0px; margin-bottom:0px; margin-left:0px; margin-right:0px; -qt-block-indent:0; text-indent:0px;"><span style=" font-size:10pt;">Note 3: Dimensioning and tolerances</span></p>\n<p style=" margin-top:0px; margin-bottom:0px; margin-left:0px; margin-right:0px; -qt-block-indent:0; text-indent:0px;"><span style=" font-size:10pt;">----------------------------------</span></p>\n<p style=" margin-top:0px; margin-bottom:0px; margin-left:0px; margin-right:0px; -qt-block-indent:0; text-indent:0px;"><span style=" font-size:10pt;">All dimensions are basic dimensions with theoretical values as defined by the 3D STEP file!</span></p>\n<p style=" margin-top:0px; margin-bottom:0px; margin-left:0px; margin-right:0px; -qt-block-indent:0; text-indent:0px;"><span style=" font-size:10pt;">All tolerances are based on ISO 2768-mK unless specified otherwise!</span></p>\n<p style=" margin-top:0px; margin-bottom:0px; margin-left:0px; margin-right:0px; -qt-block-indent:0; text-indent:0px;"><span style=" font-size:10pt;">Straightness and flatness tolerances are based on ISO 2768-mK unless specified otherwise!</span></p></body></html>
  LockPosition = false
  MaxWidth = -1
  Rotation = 0
  ScaleType = 0
  ShowFrame = false
  X = 142.164
  Y = 38.7501
FEATURE [TechDraw::DrawPage] Page002  label="PBF4_Drawing"
  KeepUpdated = true
  NextBalloonIndex = 18
  ProjectionType = 0
  Template = -> Template002
  Views = -> [ProjGroup,Dimension,Dimension001,Dimension002,RichTextAnnotation,RichTextAnnotation001]
